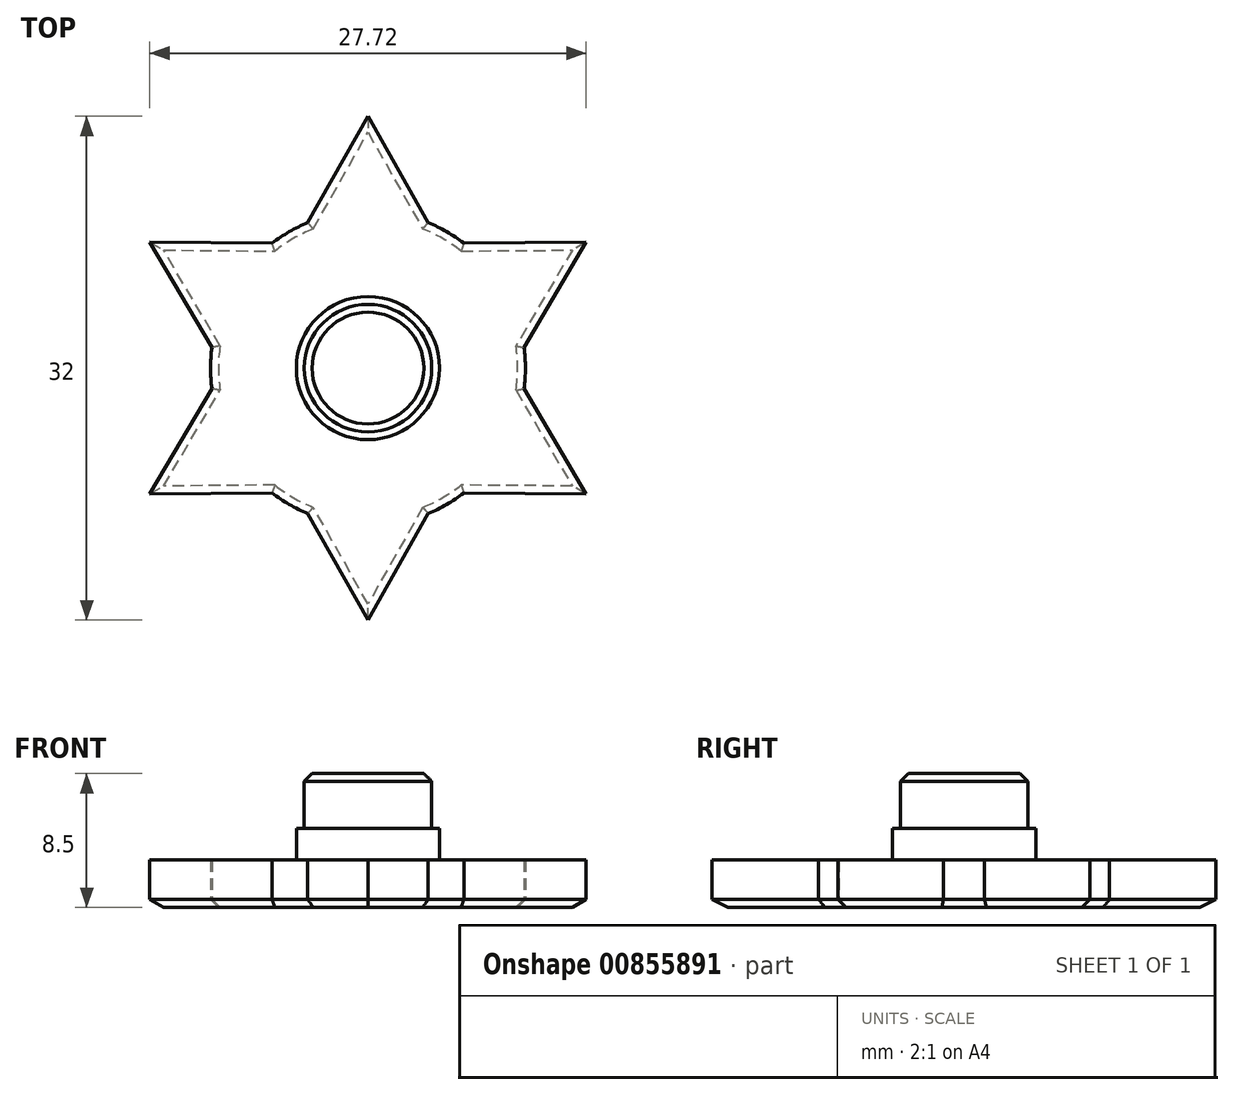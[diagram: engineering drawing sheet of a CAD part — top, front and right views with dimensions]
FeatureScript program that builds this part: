
annotation { "Feature Type Name" : "Feature", "Feature Type Description" : "" }
export const myFeature = defineFeature(function(context is Context, id is Id, definition is map)
    precondition{}
    {
        {
            var Q0;
            Q0=qCreatedBy(makeId("Top.planeOp"),FACE);
            var sketch = newSketch(context, id + "F0", { "sketchPlane" : qUnion([Q0])});
            skCircle(sketch, "E0", {"center": v(0, 0) * mm, "radius": 10 * mm});
            skLineSegment(sketch, "E1", {"start": v(0, 25) * mm, "end": v(0, -25) * mm, "construction": true});
            skLineSegment(sketch, "E2", {"start": v(-25, 0) * mm, "end": v(25, 0) * mm, "construction": true});
            skLineSegment(sketch, "E3", {"start": v(-17.68, 17.68) * mm, "end": v(0, 0) * mm, "construction": true});
            skLineSegment(sketch, "E4", {"start": v(0, 0) * mm, "end": v(17.68, -17.68) * mm, "construction": true});
            skLineSegment(sketch, "E5", {"start": v(0, 0) * mm, "end": v(17.68, 17.68) * mm, "construction": true});
            skLineSegment(sketch, "E6", {"start": v(0, 0) * mm, "end": v(-17.68, -17.68) * mm, "construction": true});
            skCircle(sketch, "E7", {"center": v(0, 0) * mm, "radius": 16 * mm, "construction": true});
            skLineSegment(sketch, "E8", {"start": v(0, 0) * mm, "end": v(-7.65, 18.48) * mm, "construction": true});
            skLineSegment(sketch, "E9", {"start": v(0, 0) * mm, "end": v(-18.48, -7.65) * mm, "construction": true});
            skLineSegment(sketch, "E10", {"start": v(0, 0) * mm, "end": v(-7.65, -18.48) * mm, "construction": true});
            skLineSegment(sketch, "E11", {"start": v(0, 0) * mm, "end": v(7.65, -18.48) * mm, "construction": true});
            skLineSegment(sketch, "E12", {"start": v(0, 0) * mm, "end": v(18.48, -7.65) * mm, "construction": true});
            skLineSegment(sketch, "E13", {"start": v(0, 0) * mm, "end": v(18.48, 7.65) * mm, "construction": true});
            skLineSegment(sketch, "E14", {"start": v(0, 0) * mm, "end": v(7.65, 18.48) * mm, "construction": true});
            skLineSegment(sketch, "E15", {"start": v(0, 0) * mm, "end": v(-18.48, 7.65) * mm, "construction": true});
            skLineSegment(sketch, "E16", {"start": v(0, 16) * mm, "end": v(-3.83, 9.24) * mm});
            skLineSegment(sketch, "E17", {"start": v(0, 16) * mm, "end": v(3.83, 9.24) * mm});
            skLineSegment(sketch, "E18.1.0", {"start": v(-13.86, 8) * mm, "end": v(-6.09, 7.93) * mm});
            skLineSegment(sketch, "E18.1.1", {"start": v(-13.86, 8) * mm, "end": v(-9.91, 1.3) * mm});
            skLineSegment(sketch, "E18.2.0", {"start": v(-13.86, -8) * mm, "end": v(-9.91, -1.3) * mm});
            skLineSegment(sketch, "E18.2.1", {"start": v(-13.86, -8) * mm, "end": v(-6.09, -7.93) * mm});
            skLineSegment(sketch, "E18.3.0", {"start": v(0, -16) * mm, "end": v(-3.83, -9.24) * mm});
            skLineSegment(sketch, "E18.3.1", {"start": v(0, -16) * mm, "end": v(3.83, -9.24) * mm});
            skLineSegment(sketch, "E18.4.0", {"start": v(13.86, -8) * mm, "end": v(6.09, -7.93) * mm});
            skLineSegment(sketch, "E18.4.1", {"start": v(13.86, -8) * mm, "end": v(9.91, -1.3) * mm});
            skLineSegment(sketch, "E18.5.0", {"start": v(13.86, 8) * mm, "end": v(9.91, 1.3) * mm});
            skLineSegment(sketch, "E18.5.1", {"start": v(13.86, 8) * mm, "end": v(6.09, 7.93) * mm});
            skSolve(sketch);
        }
        {
            var Q0;
            Q0=qSketchRegion(id+"F0",true);
            extrude(context, id + "F1", {"entities" : qUnion([Q0]), "depth" : 3 * mm, "offsetDistance" : 25 * mm});
        }
        {
            var Q0;
            Q0=makeQuery(id+"F1.opExtrude","CAP_FACE",FACE,{"disambiguationData":[OSD([sQuery(id+"F0.wireOp",EDGE,"E0")])],"isStart":false});
            var sketch = newSketch(context, id + "F2", { "sketchPlane" : qUnion([Q0])});
            skCircle(sketch, "E19", {"center": v(0, 0) * mm, "radius": 4.05 * mm});
            skSolve(sketch);
        }
        {
            var Q0;
            Q0=qSketchRegion(id+"F2",true);
            extrude(context, id + "F3", {"entities" : qUnion([Q0]), "operationType" : NewBodyOperationType.ADD, "depth" : 5.5 * mm, "offsetDistance" : 25 * mm});
        }
        {
            var Q0;
            Q0=makeQuery(id+"F3.opExtrude","CAP_EDGE",EDGE,{"disambiguationData":[OSD([sQuery(id+"F2.wireOp",EDGE,"E19")])],"isStart":false});
            var Q1;
            Q1=makeQuery(id+"F1.opExtrude","CAP_EDGE",EDGE,{"disambiguationData":[OSD([sQuery(id+"F0.wireOp",EDGE,"E18.4.0")])],"isStart":true});
            var Q2;
            {var subQ0=sQuery(id+"F0.wireOp",EDGE,"E0");Q2=makeQuery(id+"F1.opExtrude","CAP_EDGE",EDGE,{"disambiguationData":[OSD([subQ0]),TDD([makeQuery(id+"F0.imprint","IMPRINT",EDGE,{"disambiguationData":[TD([[makeQuery(id+"F0.imprint","INTERSECT",VERTEX,{"derivedFrom":[subQ0,sQuery(id+"F0.wireOp",EDGE,"E18.3.1")]}),-1.0]])],"derivedFrom":subQ0})])],"isStart":true});}
            var Q3;
            Q3=makeQuery(id+"F1.opExtrude","CAP_EDGE",EDGE,{"disambiguationData":[OSD([sQuery(id+"F0.wireOp",EDGE,"E18.3.1")])],"isStart":true});
            var Q4;
            Q4=makeQuery(id+"F1.opExtrude","CAP_EDGE",EDGE,{"disambiguationData":[OSD([sQuery(id+"F0.wireOp",EDGE,"E18.3.0")])],"isStart":true});
            var Q5;
            {var subQ0=sQuery(id+"F0.wireOp",EDGE,"E0");Q5=makeQuery(id+"F1.opExtrude","CAP_EDGE",EDGE,{"disambiguationData":[OSD([subQ0]),TDD([makeQuery(id+"F0.imprint","IMPRINT",EDGE,{"disambiguationData":[TD([[makeQuery(id+"F0.imprint","INTERSECT",VERTEX,{"derivedFrom":[subQ0,sQuery(id+"F0.wireOp",EDGE,"E18.2.1")]}),-1.0]])],"derivedFrom":subQ0})])],"isStart":true});}
            var Q6;
            Q6=makeQuery(id+"F1.opExtrude","CAP_EDGE",EDGE,{"disambiguationData":[OSD([sQuery(id+"F0.wireOp",EDGE,"E18.2.1")])],"isStart":true});
            var Q7;
            Q7=makeQuery(id+"F1.opExtrude","CAP_EDGE",EDGE,{"disambiguationData":[OSD([sQuery(id+"F0.wireOp",EDGE,"E18.2.0")])],"isStart":true});
            var Q8;
            {var subQ0=sQuery(id+"F0.wireOp",EDGE,"E0");Q8=makeQuery(id+"F1.opExtrude","CAP_EDGE",EDGE,{"disambiguationData":[OSD([subQ0]),TDD([makeQuery(id+"F0.imprint","IMPRINT",EDGE,{"disambiguationData":[TD([[makeQuery(id+"F0.imprint","INTERSECT",VERTEX,{"derivedFrom":[subQ0,sQuery(id+"F0.wireOp",EDGE,"E18.1.1")]}),-1.0]])],"derivedFrom":subQ0})])],"isStart":true});}
            var Q9;
            Q9=makeQuery(id+"F1.opExtrude","CAP_EDGE",EDGE,{"disambiguationData":[OSD([sQuery(id+"F0.wireOp",EDGE,"E18.1.1")])],"isStart":true});
            var Q10;
            Q10=makeQuery(id+"F1.opExtrude","CAP_EDGE",EDGE,{"disambiguationData":[OSD([sQuery(id+"F0.wireOp",EDGE,"E18.1.0")])],"isStart":true});
            var Q11;
            {var subQ0=sQuery(id+"F0.wireOp",EDGE,"E0");Q11=makeQuery(id+"F1.opExtrude","CAP_EDGE",EDGE,{"disambiguationData":[OSD([subQ0]),TDD([makeQuery(id+"F0.imprint","IMPRINT",EDGE,{"disambiguationData":[TD([[makeQuery(id+"F0.imprint","INTERSECT",VERTEX,{"derivedFrom":[subQ0,sQuery(id+"F0.wireOp",EDGE,"E16")]}),-1.0]])],"derivedFrom":subQ0})])],"isStart":true});}
            var Q12;
            Q12=makeQuery(id+"F1.opExtrude","CAP_EDGE",EDGE,{"disambiguationData":[OSD([sQuery(id+"F0.wireOp",EDGE,"E16")])],"isStart":true});
            var Q13;
            Q13=makeQuery(id+"F1.opExtrude","CAP_EDGE",EDGE,{"disambiguationData":[OSD([sQuery(id+"F0.wireOp",EDGE,"E17")])],"isStart":true});
            var Q14;
            {var subQ0=sQuery(id+"F0.wireOp",EDGE,"E0");Q14=makeQuery(id+"F1.opExtrude","CAP_EDGE",EDGE,{"disambiguationData":[OSD([subQ0]),TDD([makeQuery(id+"F0.imprint","IMPRINT",EDGE,{"disambiguationData":[TD([[makeQuery(id+"F0.imprint","INTERSECT",VERTEX,{"derivedFrom":[subQ0,sQuery(id+"F0.wireOp",EDGE,"E17")]}),1.0]])],"derivedFrom":subQ0})])],"isStart":true});}
            var Q15;
            Q15=makeQuery(id+"F1.opExtrude","CAP_EDGE",EDGE,{"disambiguationData":[OSD([sQuery(id+"F0.wireOp",EDGE,"E18.5.1")])],"isStart":true});
            var Q16;
            Q16=makeQuery(id+"F1.opExtrude","CAP_EDGE",EDGE,{"disambiguationData":[OSD([sQuery(id+"F0.wireOp",EDGE,"E18.5.0")])],"isStart":true});
            var Q17;
            {var subQ0=sQuery(id+"F0.wireOp",EDGE,"E0");Q17=makeQuery(id+"F1.opExtrude","CAP_EDGE",EDGE,{"disambiguationData":[OSD([subQ0]),TDD([makeQuery(id+"F0.imprint","IMPRINT",EDGE,{"disambiguationData":[TD([[makeQuery(id+"F0.imprint","INTERSECT",VERTEX,{"derivedFrom":[subQ0,sQuery(id+"F0.wireOp",EDGE,"E18.4.1")]}),-1.0]])],"derivedFrom":subQ0})])],"isStart":true});}
            var Q18;
            Q18=makeQuery(id+"F1.opExtrude","CAP_EDGE",EDGE,{"disambiguationData":[OSD([sQuery(id+"F0.wireOp",EDGE,"E18.4.1")])],"isStart":true});
            chamfer(context, id + "F4", {"entities" : qUnion([Q0, Q1, Q2, Q3, Q4, Q5, Q6, Q7, Q8, Q9, Q10, Q11, Q12, Q13, Q14, Q15, Q16, Q17, Q18]), "width" : 0.5 * mm, "tangentPropagation" : true});
        }
        {
            var Q0;
            Q0=makeQuery(id+"F1.opExtrude","CAP_FACE",FACE,{"disambiguationData":[OSD([sQuery(id+"F0.wireOp",EDGE,"E0")])],"isStart":false});
            var sketch = newSketch(context, id + "F5", { "sketchPlane" : qUnion([Q0])});
            skCircle(sketch, "E20", {"center": v(0, 0) * mm, "radius": 4.55 * mm});
            skSolve(sketch);
        }
        {
            var Q0;
            Q0=qSketchRegion(id+"F5",true);
            extrude(context, id + "F6", {"entities" : qUnion([Q0]), "operationType" : NewBodyOperationType.ADD, "depth" : 2 * mm, "offsetDistance" : 25 * mm});
        }
    });
